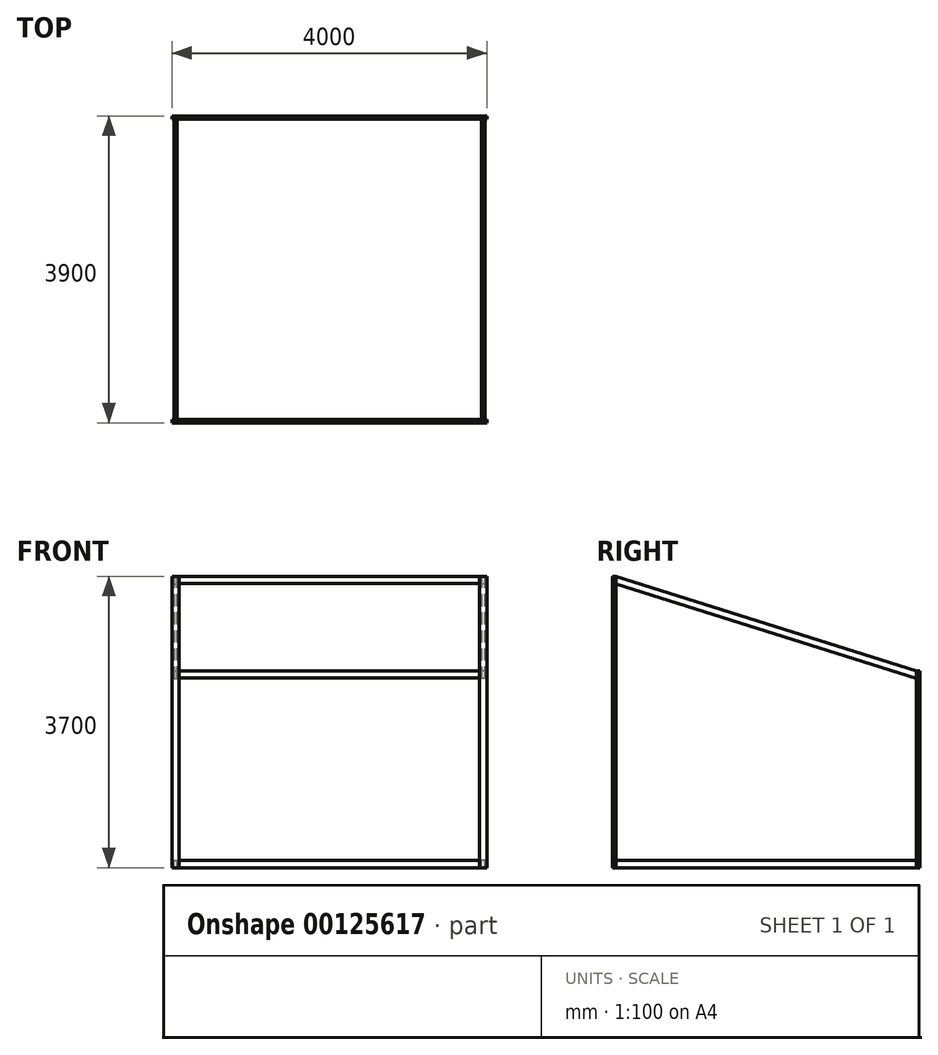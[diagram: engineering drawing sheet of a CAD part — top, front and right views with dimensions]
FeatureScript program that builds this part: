
annotation { "Feature Type Name" : "Feature", "Feature Type Description" : "" }
export const myFeature = defineFeature(function(context is Context, id is Id, definition is map)
    precondition{}
    {
        {
            var Q0;
            Q0=qCreatedBy(makeId("Front.planeOp"),FACE);
            var sketch = newSketch(context, id + "F0", { "sketchPlane" : qUnion([Q0])});
            skLineSegment(sketch, "E0.bottom", {"start": v(2000, -1850) * mm, "end": v(-2000, -1850) * mm});
            skLineSegment(sketch, "E0.top", {"start": v(2000, 1850) * mm, "end": v(-2000, 1850) * mm});
            skLineSegment(sketch, "E0.left", {"start": v(2000, -1850) * mm, "end": v(2000, 1850) * mm});
            skLineSegment(sketch, "E0.right", {"start": v(-2000, -1850) * mm, "end": v(-2000, 1850) * mm});
            skPoint(sketch, "E0.middle", {"position": v(0, 0) * mm});
            skSolve(sketch);
        }
        {
            var Q0;
            Q0=qCreatedBy(makeId("Front.planeOp"),FACE);
            var sketch = newSketch(context, id + "F1", { "sketchPlane" : qUnion([Q0])});
            skLineSegment(sketch, "E1.bottom", {"start": v(-2000, 1850) * mm, "end": v(-1910, 1850) * mm});
            skLineSegment(sketch, "E1.top", {"start": v(-2000, -1850) * mm, "end": v(-1910, -1850) * mm});
            skLineSegment(sketch, "E1.left", {"start": v(-2000, 1850) * mm, "end": v(-2000, -1850) * mm});
            skLineSegment(sketch, "E1.right", {"start": v(-1910, 1850) * mm, "end": v(-1910, -1850) * mm});
            skLineSegment(sketch, "E2", {"start": v(0, 1850) * mm, "end": v(0, -1850) * mm, "construction": true});
            skLineSegment(sketch, "E3.MirrorCS", {"start": v(2000, 1850) * mm, "end": v(1910, 1850) * mm});
            skLineSegment(sketch, "E4.MirrorCS", {"start": v(2000, -1850) * mm, "end": v(1910, -1850) * mm});
            skLineSegment(sketch, "E5.MirrorCS", {"start": v(1910, 1850) * mm, "end": v(1910, -1850) * mm});
            skLineSegment(sketch, "E6.MirrorCS", {"start": v(2000, 1850) * mm, "end": v(2000, -1850) * mm});
            skSolve(sketch);
        }
        {
            var Q0;
            Q0=qSketchRegion(id+"F1",true);
            extrude(context, id + "F2", {"entities" : qUnion([Q0]), "depth" : 40 * mm});
        }
        {
            var Q0;
            Q0=makeQuery(id+"F0.imprint","IMPRINT",FACE,{"disambiguationData":[TD([[makeQuery(id+"F0.imprint","IMPRINT",EDGE,{"derivedFrom":sQuery(id+"F0.wireOp",EDGE,"E0.bottom")}),-1.0]])]});
            var sketch = newSketch(context, id + "F3", { "sketchPlane" : qUnion([Q0])});
            skLineSegment(sketch, "E7.bottom", {"start": v(-1910, 1850) * mm, "end": v(1910, 1850) * mm});
            skLineSegment(sketch, "E7.top", {"start": v(-1910, 1760) * mm, "end": v(1910, 1760) * mm});
            skLineSegment(sketch, "E7.left", {"start": v(-1910, 1850) * mm, "end": v(-1910, 1760) * mm});
            skLineSegment(sketch, "E7.right", {"start": v(1910, 1850) * mm, "end": v(1910, 1760) * mm});
            skSolve(sketch);
        }
        {
            var Q0;
            Q0=qSketchRegion(id+"F3",true);
            extrude(context, id + "F4", {"entities" : qUnion([Q0]), "depth" : 40 * mm});
        }
        {
            var Q0;
            Q0=qCreatedBy(makeId("Right.planeOp"),FACE);
            var sketch = newSketch(context, id + "F5", { "sketchPlane" : qUnion([Q0])});
            skLineSegment(sketch, "E8", {"start": v(0, 1850) * mm, "end": v(3820, 650) * mm});
            skLineSegment(sketch, "E9", {"start": v(3820, 650) * mm, "end": v(3820, 555.66) * mm});
            skLineSegment(sketch, "E10", {"start": v(3820, 555.66) * mm, "end": v(0, 1755.66) * mm});
            skLineSegment(sketch, "E11", {"start": v(0, 1755.66) * mm, "end": v(0, 1850) * mm});
            skLineSegment(sketch, "E12.bottom", {"start": v(3820, -1850) * mm, "end": v(3860, -1850) * mm});
            skLineSegment(sketch, "E12.top", {"start": v(3820, 650) * mm, "end": v(3860, 650) * mm});
            skLineSegment(sketch, "E12.left", {"start": v(3820, -1850) * mm, "end": v(3820, 650) * mm});
            skLineSegment(sketch, "E12.right", {"start": v(3860, -1850) * mm, "end": v(3860, 650) * mm});
            skLineSegment(sketch, "E13.bottom", {"start": v(3820, -1850) * mm, "end": v(0, -1850) * mm});
            skLineSegment(sketch, "E13.top", {"start": v(3820, -1760) * mm, "end": v(0, -1760) * mm});
            skLineSegment(sketch, "E13.left", {"start": v(3820, -1850) * mm, "end": v(3820, -1760) * mm});
            skLineSegment(sketch, "E13.right", {"start": v(0, -1850) * mm, "end": v(0, -1760) * mm});
            skLineSegment(sketch, "E14", {"start": v(2620, 932.63) * mm, "end": v(2620, -1760) * mm});
            skLineSegment(sketch, "E15", {"start": v(2620, -1760) * mm, "end": v(2620, 740) * mm});
            skLineSegment(sketch, "E16", {"start": v(2620, 740) * mm, "end": v(3820, 555.66) * mm});
            skLineSegment(sketch, "E17", {"start": v(2620, 740) * mm, "end": v(-38.63, 1148.4) * mm});
            skSolve(sketch);
        }
        {
            var Q0;
            Q0=makeQuery(id+"F2.opExtrude","SWEPT_FACE",FACE,{"disambiguationData":[OSD([sQuery(id+"F1.wireOp",EDGE,"E1.left")])]});
            cPlane(context, id + "F6", {"entities" : qUnion([Q0]), "cplaneType" : CPlaneType.OFFSET, "offset" : 45 * mm, "oppositeDirection" : true, "width" : 150 * mm, "height" : 150 * mm});
        }
        {
            var Q0;
            Q0=qCreatedBy(id+"F6.planeOp",FACE);
            var sketch = newSketch(context, id + "F7", { "sketchPlane" : qUnion([Q0])});
            skLineSegment(sketch, "E18.0", {"start": v(0, 1850) * mm, "end": v(-3820, 650) * mm});
            skLineSegment(sketch, "E18.1", {"start": v(0, 1755.66) * mm, "end": v(0, 1850) * mm});
            skLineSegment(sketch, "E18.2", {"start": v(-3820, 555.66) * mm, "end": v(0, 1755.66) * mm});
            skPoint(sketch, "E18.3", {"position": v(-3820, 555.66) * mm});
            skLineSegment(sketch, "E19", {"start": v(-3820, 650) * mm, "end": v(-3820, 555.66) * mm});
            skLineSegment(sketch, "E20.0", {"start": v(-3820, -1850) * mm, "end": v(-3820, -1760) * mm});
            skLineSegment(sketch, "E20.1", {"start": v(-3820, -1760) * mm, "end": v(0, -1760) * mm});
            skLineSegment(sketch, "E20.2", {"start": v(-3820, -1850) * mm, "end": v(0, -1850) * mm});
            skLineSegment(sketch, "E20.3", {"start": v(0, -1850) * mm, "end": v(0, -1760) * mm});
            skSolve(sketch);
        }
        {
            var Q0;
            Q0=qSketchRegion(id+"F7",true);
            extrude(context, id + "F8", {"entities" : qUnion([Q0]), "depth" : 20 * mm, "hasSecondDirection" : true, "secondDirectionOppositeDirection" : true, "secondDirectionDepth" : 20 * mm});
        }
        {
            var Q0;
            Q0=makeQuery(id+"F8.opExtrude","SWEPT_BODY",BODY,{"disambiguationData":[OSD([sQuery(id+"F7.wireOp",EDGE,"E18.0"),sQuery(id+"F7.wireOp",EDGE,"E18.1"),sQuery(id+"F7.wireOp",EDGE,"E18.2"),sQuery(id+"F7.wireOp",EDGE,"E19")])]});
            var Q1;
            Q1=makeQuery(id+"F8.opExtrude","SWEPT_BODY",BODY,{"disambiguationData":[OSD([sQuery(id+"F7.wireOp",EDGE,"E20.0"),sQuery(id+"F7.wireOp",EDGE,"E20.1"),sQuery(id+"F7.wireOp",EDGE,"E20.2"),sQuery(id+"F7.wireOp",EDGE,"E20.3")])]});
            var Q2;
            Q2=qCreatedBy(makeId("Right.planeOp"),FACE);
            mirror(context, id + "F9", {"operationType" : NewBodyOperationType.ADD, "entities" : qUnion([Q0, Q1]), "mirrorPlane" : qUnion([Q2])});
        }
        {
            var Q0;
            Q0=makeQuery(id+"F8.opExtrude","SWEPT_FACE",FACE,{"disambiguationData":[OSD([sQuery(id+"F7.wireOp",EDGE,"E19")])]});
            var sketch = newSketch(context, id + "F10", { "sketchPlane" : qUnion([Q0])});
            skLineSegment(sketch, "E21.bottom", {"start": v(-2000, -1850) * mm, "end": v(-1910, -1850) * mm});
            skLineSegment(sketch, "E21.top", {"start": v(-2000, 650) * mm, "end": v(-1910, 650) * mm});
            skLineSegment(sketch, "E21.left", {"start": v(-2000, -1850) * mm, "end": v(-2000, 650) * mm});
            skLineSegment(sketch, "E21.right", {"start": v(-1910, -1850) * mm, "end": v(-1910, 650) * mm});
            skLineSegment(sketch, "E22.0", {"start": v(0, -1850) * mm, "end": v(0, 650) * mm, "construction": true});
            skLineSegment(sketch, "E23.MirrorCS", {"start": v(2000, 650) * mm, "end": v(1910, 650) * mm});
            skLineSegment(sketch, "E24.MirrorCS", {"start": v(2000, -1850) * mm, "end": v(1910, -1850) * mm});
            skLineSegment(sketch, "E25.MirrorCS", {"start": v(2000, -1850) * mm, "end": v(2000, 650) * mm});
            skLineSegment(sketch, "E26.MirrorCS", {"start": v(1910, -1850) * mm, "end": v(1910, 650) * mm});
            skLineSegment(sketch, "E27", {"start": v(0, -600) * mm, "end": v(1910, -600) * mm, "construction": true});
            skLineSegment(sketch, "E28.bottom", {"start": v(1910, 560) * mm, "end": v(-1910, 560) * mm});
            skLineSegment(sketch, "E28.top", {"start": v(1910, 650) * mm, "end": v(-1910, 650) * mm});
            skLineSegment(sketch, "E28.left", {"start": v(1910, 560) * mm, "end": v(1910, 650) * mm});
            skLineSegment(sketch, "E28.right", {"start": v(-1910, 560) * mm, "end": v(-1910, 650) * mm});
            skPoint(sketch, "E28.middle", {"position": v(0, 605) * mm});
            skLineSegment(sketch, "E29.MirrorCS", {"start": v(-1910, -1760) * mm, "end": v(-1910, -1850) * mm});
            skLineSegment(sketch, "E30.MirrorCS", {"start": v(1910, -1760) * mm, "end": v(1910, -1850) * mm});
            skPoint(sketch, "E31.MirrorP", {"position": v(0, -1805) * mm});
            skLineSegment(sketch, "E32.MirrorCS", {"start": v(1910, -1760) * mm, "end": v(-1910, -1760) * mm});
            skLineSegment(sketch, "E33.MirrorCS", {"start": v(1910, -1850) * mm, "end": v(-1910, -1850) * mm});
            skSolve(sketch);
        }
        {
            var Q0;
            Q0=qSketchRegion(id+"F10",true);
            extrude(context, id + "F11", {"entities" : qUnion([Q0]), "depth" : 40 * mm});
        }
    });
